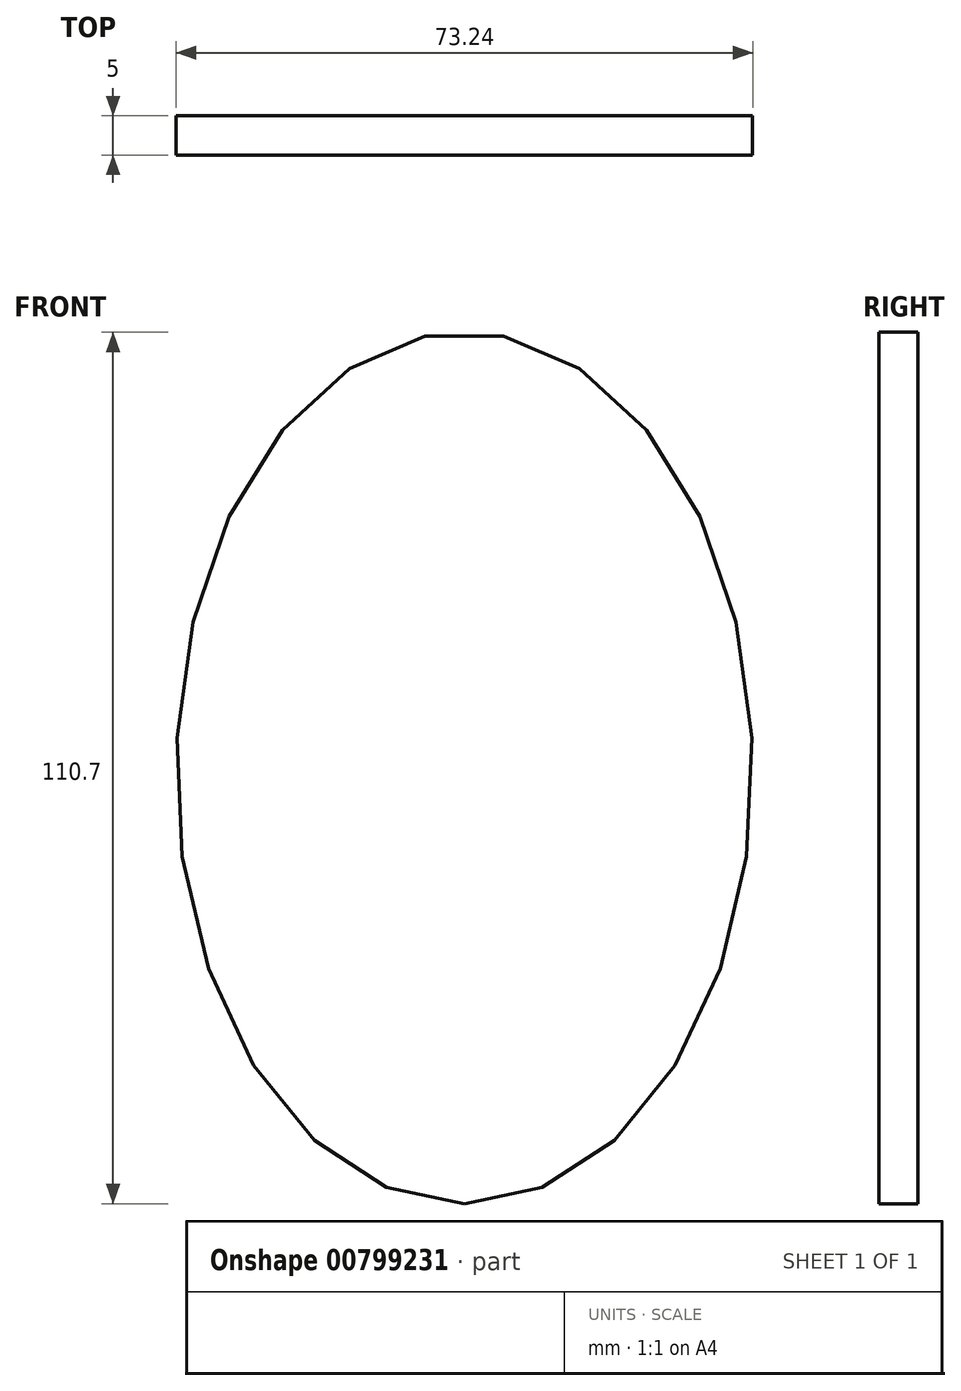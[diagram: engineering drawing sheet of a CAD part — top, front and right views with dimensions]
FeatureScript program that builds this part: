
annotation { "Feature Type Name" : "Feature", "Feature Type Description" : "" }
export const myFeature = defineFeature(function(context is Context, id is Id, definition is map)
    precondition{}
    {
        {
            var Q0;
            Q0=qCreatedBy(makeId("Front.planeOp"),FACE);
            var sketch = newSketch(context, id + "F0", { "sketchPlane" : qUnion([Q0])});
            skEllipse(sketch, "E0", {"center": v(0, 0) * mm, "majorRadius": 55.35 * mm, "minorRadius": 36.62 * mm, "majorAxis": v(0, -1)});
            skSolve(sketch);
        }
        {
            var Q0;
            Q0 = qSketchRegion(id + "F0", true);
            extrude(context, id + "F1", {"entities" : qUnion([Q0]), "depth" : 5 * mm, "offsetDistance" : 25 * mm});
        }
    });
